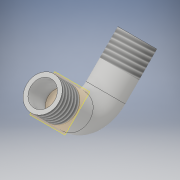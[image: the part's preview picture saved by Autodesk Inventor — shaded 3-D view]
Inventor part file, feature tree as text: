
AUTODESK INVENTOR PART (.ipt)
format: ipt  version: 2018 (Build 220112000, 112)  size: 186,880 bytes
history: native  units: in
note: dims shown in document units (in); Inventor stores cm internally (conversion verified against a paired STEP export)
features: sketch x3, extrude x2, thread x2, other x1, plane x1, chamfer x1
ambient origin geometry x8: Origin, YZ Plane, XZ Plane, XY Plane, X Axis, Y Axis, Z Axis, Center Point
bodies: Solid1 (feature_tree)
feature tree (10):
  extrude  "Extrusion1"  Depth=0.476in
  other  "Bend Part1"
  thread  "Thread1"  [1 undecoded]
  thread  "Thread2"  [1 undecoded]
  plane  "Work Plane1"
  extrude  "Extrusion2"  Depth=0.5in TaperAngle=0.0deg
  chamfer  "Chamfer1"  Distance=0.5in
  sketch  "Sketch1"  dims[d0=0.6345in d1=0.476in d2=2.457in d3=0.0in d4=1.24in]
  sketch  "Sketch2"  dims[d5=0.45in d6=90.0deg d7=0.5in d8=0.0in d9=0.5in d10=0.0in]
  sketch  "Sketch3"  dims[d11=-0.48in d12=0.193in d13=0.75in d14=0.0in d15=0.125in d16=0.125in d17=45.0deg]
note: 2 required parameter values undecoded (feature->parameter linkage not recoverable at this tier; creation-order binding heuristic only, values carry confidence <= 0.55)
